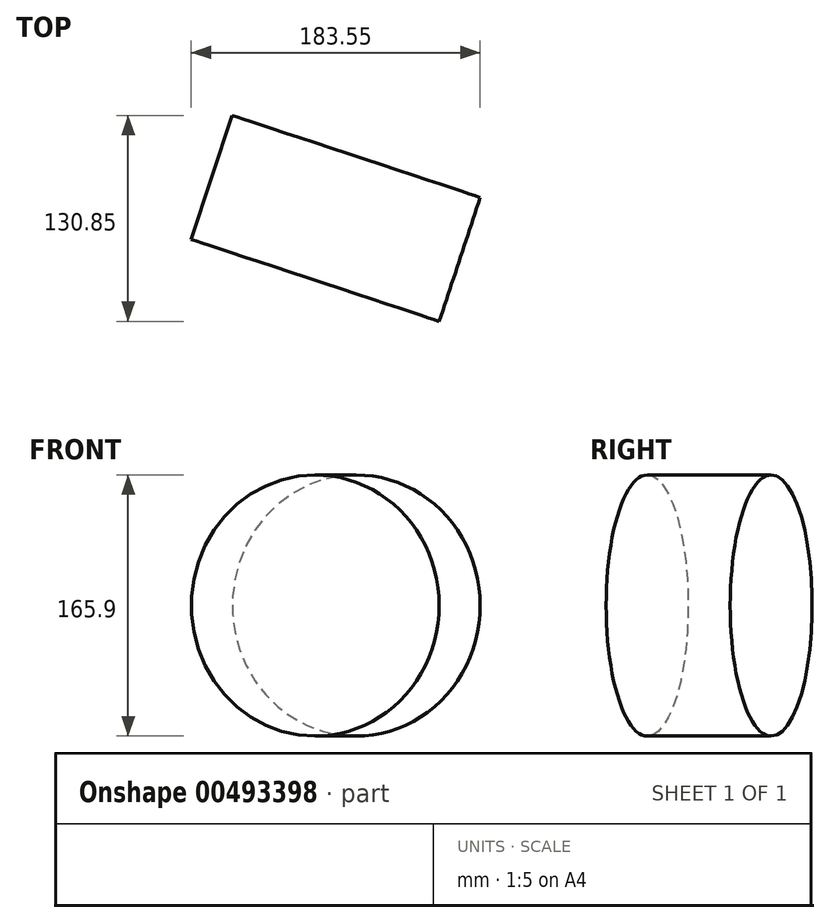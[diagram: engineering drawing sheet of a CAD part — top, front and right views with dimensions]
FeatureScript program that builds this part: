
annotation { "Feature Type Name" : "Feature", "Feature Type Description" : "" }
export const myFeature = defineFeature(function(context is Context, id is Id, definition is map)
    precondition{}
    {
        {
            var Q0;
            Q0=qCreatedBy(makeId("Top.planeOp"),FACE);
            var sketch = newSketch(context, id + "F0", { "sketchPlane" : qUnion([Q0])});
            skCircle(sketch, "E0.cCircle", {"center": v(0, 0) * mm, "radius": 58.65 * mm, "construction": true});
            skLineSegment(sketch, "E0.0", {"start": v(-26.35, 52.4) * mm, "end": v(52.4, 26.35) * mm});
            skLineSegment(sketch, "E0.1", {"start": v(52.4, 26.35) * mm, "end": v(26.35, -52.4) * mm});
            skLineSegment(sketch, "E0.2", {"start": v(26.35, -52.4) * mm, "end": v(-52.4, -26.35) * mm});
            skLineSegment(sketch, "E0.3", {"start": v(-52.4, -26.35) * mm, "end": v(-26.35, 52.4) * mm});
            skSolve(sketch);
        }
        {
            var Q0;
            Q0=makeQuery(id+"F0.imprint","IMPRINT",FACE,{"disambiguationData":[TD([[makeQuery(id+"F0.imprint","IMPRINT",EDGE,{"derivedFrom":sQuery(id+"F0.wireOp",EDGE,"E0.0")}),-1.0]])]});
            var Q1;
            Q1=sQuery(id+"F0.wireOp",EDGE,"E0.3");
            revolve(context, id + "F1", {"entities" : qUnion([Q0]), "axis" : qUnion([Q1]), "revolveType" : RevolveType.FULL});
        }
    });
